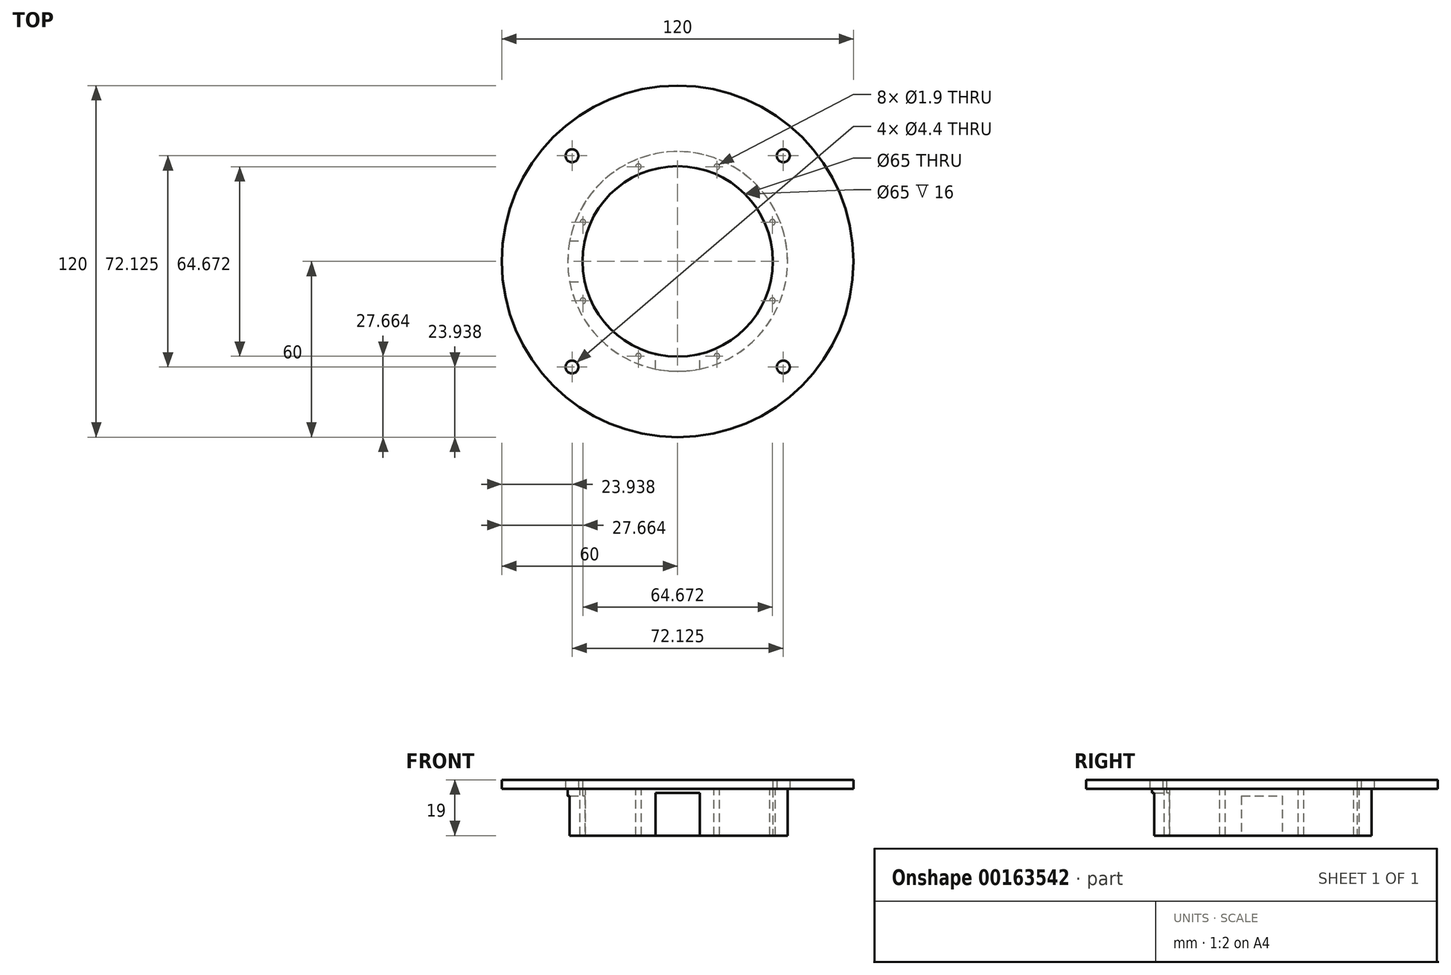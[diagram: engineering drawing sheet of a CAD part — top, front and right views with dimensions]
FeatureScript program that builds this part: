
annotation { "Feature Type Name" : "Feature", "Feature Type Description" : "" }
export const myFeature = defineFeature(function(context is Context, id is Id, definition is map)
    precondition{}
    {
        {
            var Q0;
            Q0=qCreatedBy(makeId("Top.planeOp"),FACE);
            var sketch = newSketch(context, id + "F0", { "sketchPlane" : qUnion([Q0])});
            skCircle(sketch, "E0", {"center": v(0, 0) * mm, "radius": 37.5 * mm});
            skCircle(sketch, "E1", {"center": v(0, 0) * mm, "radius": 32.5 * mm});
            skCircle(sketch, "E2", {"center": v(0, 0) * mm, "radius": 35 * mm, "construction": true});
            skPoint(sketch, "E3", {"position": v(-35, 0) * mm});
            skPoint(sketch, "E4", {"position": v(0, 35) * mm});
            skPoint(sketch, "E5", {"position": v(35, 0) * mm});
            skPoint(sketch, "E6", {"position": v(0, -35) * mm});
            skSolve(sketch);
        }
        {
            var Q0;
            Q0=makeQuery(id+"F0.imprint","IMPRINT",FACE,{"disambiguationData":[TD([[makeQuery(id+"F0.imprint","IMPRINT",EDGE,{"derivedFrom":sQuery(id+"F0.wireOp",EDGE,"E0")}),1.0]])]});
            extrude(context, id + "F1", {"entities" : qUnion([Q0]), "depth" : 16 * mm});
        }
        {
            var Q0;
            Q0=qCreatedBy(makeId("Right.planeOp"),FACE);
            var sketch = newSketch(context, id + "F2", { "sketchPlane" : qUnion([Q0])});
            skLineSegment(sketch, "E7.bottom", {"start": v(-7, 0) * mm, "end": v(7, 0) * mm});
            skLineSegment(sketch, "E7.top", {"start": v(-7, 13.5) * mm, "end": v(7, 13.5) * mm});
            skLineSegment(sketch, "E7.left", {"start": v(-7, 0) * mm, "end": v(-7, 13.5) * mm});
            skLineSegment(sketch, "E7.right", {"start": v(7, 0) * mm, "end": v(7, 13.5) * mm});
            skSolve(sketch);
        }
        {
            var Q0;
            Q0 = qSketchRegion(id + "F2", true);
            extrude(context, id + "F3", {"entities" : qUnion([Q0]), "operationType" : NewBodyOperationType.REMOVE, "endBound" : BoundingType.THROUGH_ALL, "oppositeDirection" : true, "depth" : 50 * mm});
        }
        {
            var Q0;
            Q0=qCreatedBy(makeId("Front.planeOp"),FACE);
            var sketch = newSketch(context, id + "F4", { "sketchPlane" : qUnion([Q0])});
            skLineSegment(sketch, "E8.bottom", {"start": v(-7.5, 0) * mm, "end": v(7.5, 0) * mm});
            skLineSegment(sketch, "E8.top", {"start": v(-7.5, 14.5) * mm, "end": v(7.5, 14.5) * mm});
            skLineSegment(sketch, "E8.left", {"start": v(-7.5, 0) * mm, "end": v(-7.5, 14.5) * mm});
            skLineSegment(sketch, "E8.right", {"start": v(7.5, 0) * mm, "end": v(7.5, 14.5) * mm});
            skSolve(sketch);
        }
        {
            var Q0;
            Q0 = qSketchRegion(id + "F4", true);
            extrude(context, id + "F5", {"entities" : qUnion([Q0]), "operationType" : NewBodyOperationType.REMOVE, "depth" : 50 * mm});
        }
        {
            var Q0;
            Q0=makeQuery(id+"F1.opExtrude","CAP_FACE",FACE,{"disambiguationData":[OSD([sQuery(id+"F0.wireOp",EDGE,"E0"),sQuery(id+"F0.wireOp",EDGE,"E1")])],"isStart":false});
            var sketch = newSketch(context, id + "F6", { "sketchPlane" : qUnion([Q0])});
            skLineSegment(sketch, "E9", {"start": v(0, 0) * mm, "end": v(-52.7, 21.83) * mm, "construction": true});
            skLineSegment(sketch, "E10", {"start": v(0, 0) * mm, "end": v(21.75, 52.51) * mm, "construction": true});
            skLineSegment(sketch, "E11", {"start": v(0, 0) * mm, "end": v(52.99, -21.95) * mm, "construction": true});
            skLineSegment(sketch, "E12", {"start": v(0, 0) * mm, "end": v(-21.6, -52.13) * mm, "construction": true});
            skCircle(sketch, "E13", {"center": v(0, 0) * mm, "radius": 35 * mm, "construction": true});
            skPoint(sketch, "E14", {"position": v(-32.34, 13.4) * mm});
            skPoint(sketch, "E15", {"position": v(13.4, 32.34) * mm});
            skPoint(sketch, "E16", {"position": v(32.34, -13.4) * mm});
            skPoint(sketch, "E17", {"position": v(-13.4, -32.34) * mm});
            skCircle(sketch, "E18", {"center": v(0, 0) * mm, "radius": 60 * mm});
            skCircle(sketch, "E19", {"center": v(0, 0) * mm, "radius": 51 * mm, "construction": true});
            skPoint(sketch, "E20", {"position": v(-47.12, 19.52) * mm});
            skPoint(sketch, "E21", {"position": v(19.52, 47.12) * mm});
            skPoint(sketch, "E22", {"position": v(47.12, -19.52) * mm});
            skPoint(sketch, "E23", {"position": v(-19.52, -47.12) * mm});
            skLineSegment(sketch, "E24", {"start": v(-40.26, 40.26) * mm, "end": v(0, 0) * mm, "construction": true});
            skLineSegment(sketch, "E25", {"start": v(0, 0) * mm, "end": v(39.75, 39.75) * mm, "construction": true});
            skLineSegment(sketch, "E26", {"start": v(39.75, 39.75) * mm, "end": v(0, 0) * mm, "construction": true});
            skLineSegment(sketch, "E27", {"start": v(0, 0) * mm, "end": v(42.43, -42.43) * mm, "construction": true});
            skLineSegment(sketch, "E28", {"start": v(42.43, -42.43) * mm, "end": v(0, 0) * mm, "construction": true});
            skLineSegment(sketch, "E29", {"start": v(0, 0) * mm, "end": v(-42.43, -42.43) * mm, "construction": true});
            skPoint(sketch, "E30", {"position": v(-36.06, 36.06) * mm});
            skPoint(sketch, "E31", {"position": v(36.06, 36.06) * mm});
            skPoint(sketch, "E32", {"position": v(36.06, -36.06) * mm});
            skPoint(sketch, "E33", {"position": v(-36.06, -36.06) * mm});
            skLineSegment(sketch, "E34", {"start": v(0, 0) * mm, "end": v(-22.96, 55.43) * mm, "construction": true});
            skLineSegment(sketch, "E35", {"start": v(-22.96, 55.43) * mm, "end": v(0, 0) * mm, "construction": true});
            skLineSegment(sketch, "E36", {"start": v(55.43, 22.96) * mm, "end": v(0, 0) * mm, "construction": true});
            skLineSegment(sketch, "E37", {"start": v(0, 0) * mm, "end": v(22.96, -55.43) * mm, "construction": true});
            skLineSegment(sketch, "E38", {"start": v(-55.43, -22.96) * mm, "end": v(0, 0) * mm, "construction": true});
            skPoint(sketch, "E39", {"position": v(-13.4, 32.34) * mm});
            skPoint(sketch, "E40", {"position": v(32.34, 13.4) * mm});
            skPoint(sketch, "E41", {"position": v(-32.34, -13.4) * mm});
            skPoint(sketch, "E42", {"position": v(13.4, -32.34) * mm});
            skSolve(sketch);
        }
        {
            var Q0;
            Q0=makeQuery(id+"F6.imprint","IMPRINT",FACE,{"disambiguationData":[TD([[makeQuery(id+"F6.imprint","IMPRINT",EDGE,{"derivedFrom":makeQuery(id+"F1.opExtrude","CAP_EDGE",EDGE,{"disambiguationData":[OSD([sQuery(id+"F0.wireOp",EDGE,"E0")])],"isStart":false})}),1.0]])]});
            var Q1;
            Q1=makeQuery(id+"F6.imprint","IMPRINT",FACE,{"disambiguationData":[TD([[makeQuery(id+"F6.imprint","IMPRINT",EDGE,{"derivedFrom":sQuery(id+"F6.wireOp",EDGE,"E18")}),1.0]])]});
            var Q2;
            Q2=sQuery(id+"F6.wireOp",EDGE,"E18");
            extrude(context, id + "F7", {"entities" : qUnion([Q0, Q1]), "surfaceEntities" : qUnion([Q2]), "depth" : 3 * mm});
        }
        {
            var Q0;
            Q0=sQuery(id+"F6.wireOp",VERTEX,"E16");
            var Q1;
            Q1=sQuery(id+"F6.wireOp",VERTEX,"E15");
            var Q2;
            Q2=sQuery(id+"F6.wireOp",VERTEX,"E17");
            var Q3;
            Q3=sQuery(id+"F6.wireOp",VERTEX,"E14");
            var Q4;
            Q4=sQuery(id+"F6.wireOp",VERTEX,"E39");
            var Q5;
            Q5=sQuery(id+"F6.wireOp",VERTEX,"E40");
            var Q6;
            Q6=sQuery(id+"F6.wireOp",VERTEX,"E42");
            var Q7;
            Q7=sQuery(id+"F6.wireOp",VERTEX,"E41");
            var Q8;
            Q8=makeQuery(id+"F1.opExtrude","SWEPT_BODY",BODY,{"disambiguationData":[OSD([sQuery(id+"F0.wireOp",EDGE,"E0"),sQuery(id+"F0.wireOp",EDGE,"E1")])]});
            hole(context, id + "F8", {"style" : HoleStyle.SIMPLE, "endStyle" : HoleEndStyle.BLIND, "holeDiameter" : 1.9 * mm, "holeDepth" : 50 * mm, "locations" : qUnion([Q0, Q1, Q2, Q3, Q4, Q5, Q6, Q7]), "scope" : qUnion([Q8])});
        }
        {
            var Q0;
            Q0=sQuery(id+"F6.wireOp",VERTEX,"E30");
            var Q1;
            Q1=sQuery(id+"F6.wireOp",VERTEX,"E31");
            var Q2;
            Q2=sQuery(id+"F6.wireOp",VERTEX,"E32");
            var Q3;
            Q3=sQuery(id+"F6.wireOp",VERTEX,"E33");
            var Q4;
            Q4=makeQuery(id+"F7.opExtrude","SWEPT_BODY",BODY,{"disambiguationData":[OSD([sQuery(id+"F0.wireOp",EDGE,"E1"),sQuery(id+"F6.wireOp",EDGE,"E18")])]});
            hole(context, id + "F9", {"style" : HoleStyle.SIMPLE, "endStyle" : HoleEndStyle.BLIND, "oppositeDirection" : true, "standardTappedOrClearance" : lookupTablePath({ "standard" : "ISO", "fit" : "Normal", "size" : "M4", "type" : "Clearance" }), "standardBlindInLast" : lookupTablePath({ "fit" : "Standard", "standard" : "ISO", "size" : "M4", "type" : "Clearance" }), "holeDiameter" : 4.4 * mm, "holeDepth" : 50 * mm, "startFromSketch" : true, "locations" : qUnion([Q0, Q1, Q2, Q3]), "scope" : qUnion([Q4])});
        }
    });
